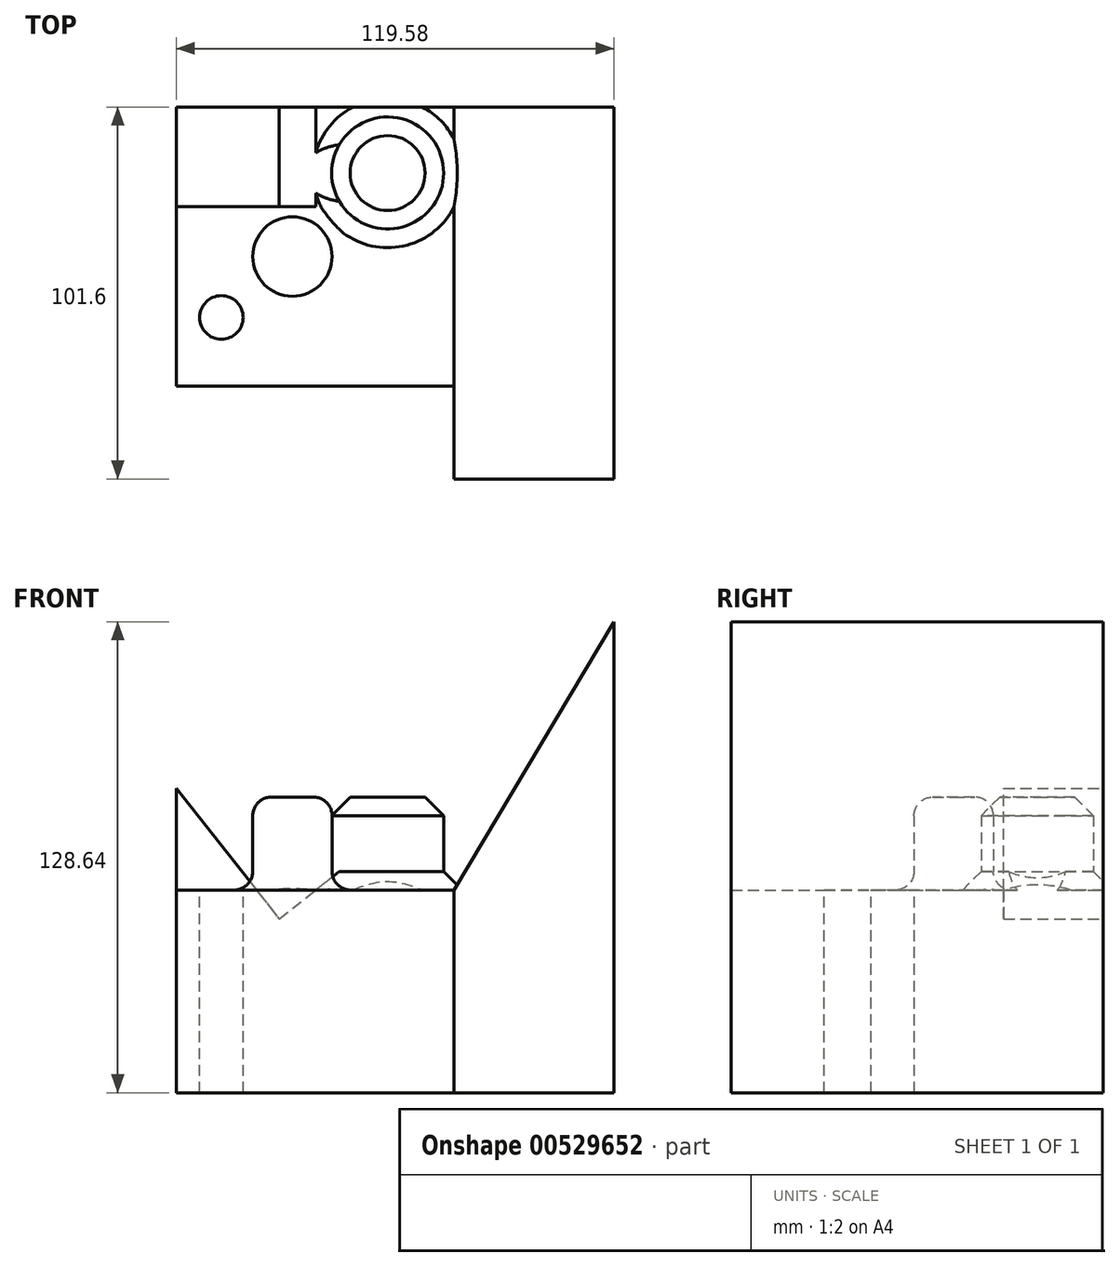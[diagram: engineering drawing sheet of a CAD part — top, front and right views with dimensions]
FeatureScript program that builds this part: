
annotation { "Feature Type Name" : "Feature", "Feature Type Description" : "" }
export const myFeature = defineFeature(function(context is Context, id is Id, definition is map)
    precondition{}
    {
        {
            var Q0;
            Q0=qCreatedBy(makeId("Front.planeOp"),FACE);
            var sketch = newSketch(context, id + "F0", { "sketchPlane" : qUnion([Q0])});
            skLineSegment(sketch, "E0", {"start": v(0, 0) * mm, "end": v(43.67, 73.3) * mm});
            skLineSegment(sketch, "E1", {"start": v(43.67, 73.3) * mm, "end": v(43.67, -55.35) * mm});
            skLineSegment(sketch, "E2", {"start": v(43.67, -55.35) * mm, "end": v(-75.9, -55.35) * mm});
            skLineSegment(sketch, "E3", {"start": v(-75.9, -55.35) * mm, "end": v(-75.9, 48.22) * mm});
            skLineSegment(sketch, "E4", {"start": v(-75.9, 48.22) * mm, "end": v(-37.8, 0) * mm});
            skLineSegment(sketch, "E5", {"start": v(-37.8, 0) * mm, "end": v(0, 0) * mm});
            skSolve(sketch);
        }
        {
            var Q0;
            Q0=makeQuery(id+"F0.imprint","IMPRINT",FACE,{"disambiguationData":[TD([[makeQuery(id+"F0.imprint","IMPRINT",EDGE,{"derivedFrom":sQuery(id+"F0.wireOp",EDGE,"E0")}),-1.0]])]});
            extrude(context, id + "F1", {"entities" : qUnion([Q0]), "depth" : 76.2 * mm, "offsetDistance" : 25.4 * mm});
        }
        {
            var Q0;
            Q0=makeQuery(id+"F1.opExtrude","CAP_FACE",FACE,{"disambiguationData":[OSD([sQuery(id+"F0.wireOp",EDGE,"E0"),sQuery(id+"F0.wireOp",EDGE,"E1"),sQuery(id+"F0.wireOp",EDGE,"E2"),sQuery(id+"F0.wireOp",EDGE,"E3"),sQuery(id+"F0.wireOp",EDGE,"E4"),sQuery(id+"F0.wireOp",EDGE,"E5")])],"isStart":false});
            var sketch = newSketch(context, id + "F2", { "sketchPlane" : qUnion([Q0])});
            skLineSegment(sketch, "E6", {"start": v(0, 0) * mm, "end": v(0, -55.35) * mm});
            skLineSegment(sketch, "E7", {"start": v(-37.8, 0) * mm, "end": v(-75.9, 0) * mm});
            skSolve(sketch);
        }
        {
            var Q0;
            {var subQ0=sQuery(id+"F2.wireOp",EDGE,"E6");Q0=makeQuery(id+"F2.imprint","IMPRINT",FACE,{"disambiguationData":[TD([[makeQuery(id+"F2.imprint","IMPRINT",EDGE,{"derivedFrom":subQ0}),1.0]])]});}
            extrude(context, id + "F3", {"entities" : qUnion([Q0]), "operationType" : NewBodyOperationType.ADD, "depth" : 25.4 * mm, "offsetDistance" : 25.4 * mm});
        }
        {
            var Q0;
            Q0=makeQuery(id+"F1.opExtrude","CAP_FACE",FACE,{"disambiguationData":[OSD([sQuery(id+"F0.wireOp",EDGE,"E0"),sQuery(id+"F0.wireOp",EDGE,"E1"),sQuery(id+"F0.wireOp",EDGE,"E2"),sQuery(id+"F0.wireOp",EDGE,"E3"),sQuery(id+"F0.wireOp",EDGE,"E4"),sQuery(id+"F0.wireOp",EDGE,"E5")])],"isStart":false});
            var sketch = newSketch(context, id + "F4", { "sketchPlane" : qUnion([Q0])});
            skLineSegment(sketch, "E8", {"start": v(-37.8, 0) * mm, "end": v(-75.9, 0) * mm});
            skSolve(sketch);
        }
        {
            var Q0;
            {var subQ0=sQuery(id+"F4.wireOp",EDGE,"E8");Q0=makeQuery(id+"F4.imprint","IMPRINT",FACE,{"disambiguationData":[TD([[makeQuery(id+"F4.imprint","IMPRINT",EDGE,{"derivedFrom":subQ0}),-1.0]])]});}
            extrude(context, id + "F5", {"entities" : qUnion([Q0]), "operationType" : NewBodyOperationType.REMOVE, "oppositeDirection" : true, "depth" : 49.02 * mm, "offsetDistance" : 25.4 * mm});
        }
        {
            var Q0;
            Q0=makeQuery(id+"F5.boolean.opBoolean","MERGE",FACE,{"derivedFrom":[makeQuery(id+"F1.opExtrude","SWEPT_FACE",FACE,{"disambiguationData":[OSD([sQuery(id+"F0.wireOp",EDGE,"E5")])]}),makeQuery(id+"F5.opExtrude","SWEPT_FACE",FACE,{"disambiguationData":[OSD([sQuery(id+"F4.wireOp",EDGE,"E8")])]})]});
            var sketch = newSketch(context, id + "F6", { "sketchPlane" : qUnion([Q0])});
            skCircle(sketch, "E9", {"center": v(-44.18, -40.85) * mm, "radius": 10.84 * mm});
            skCircle(sketch, "E10", {"center": v(-18.17, -18.04) * mm, "radius": 15.3 * mm});
            skCircle(sketch, "E11", {"center": v(-63.59, -57.5) * mm, "radius": 5.95 * mm});
            skSolve(sketch);
        }
        {
            var Q0;
            Q0=makeQuery(id+"F6.imprint","IMPRINT",FACE,{"disambiguationData":[TD([[makeQuery(id+"F6.imprint","IMPRINT",EDGE,{"derivedFrom":sQuery(id+"F6.wireOp",EDGE,"E10")}),1.0]])]});
            var Q1;
            Q1=makeQuery(id+"F6.imprint","IMPRINT",FACE,{"disambiguationData":[TD([[makeQuery(id+"F6.imprint","IMPRINT",EDGE,{"derivedFrom":sQuery(id+"F6.wireOp",EDGE,"E9")}),1.0]])]});
            var Q2;
            Q2=makeQuery(id+"F6.imprint","IMPRINT",FACE,{"disambiguationData":[TD([[makeQuery(id+"F6.imprint","IMPRINT",EDGE,{"derivedFrom":sQuery(id+"F6.wireOp",EDGE,"E11")}),1.0]])]});
            extrude(context, id + "F7", {"entities" : qUnion([Q0, Q1, Q2]), "operationType" : NewBodyOperationType.ADD, "depth" : 25.4 * mm, "offsetDistance" : 25.4 * mm});
        }
        {
            var Q0;
            Q0=makeQuery(id+"F1.opExtrude","SWEPT_FACE",FACE,{"disambiguationData":[OSD([sQuery(id+"F0.wireOp",EDGE,"E4")])]});
            extrude(context, id + "F8", {"entities" : qUnion([Q0]), "operationType" : NewBodyOperationType.REMOVE, "oppositeDirection" : true, "depth" : 12.7 * mm, "offsetDistance" : 25.4 * mm});
        }
        {
            var Q0;
            Q0=makeQuery(id+"F7.opExtrude","CAP_FACE",FACE,{"disambiguationData":[OSD([sQuery(id+"F6.wireOp",EDGE,"E11")])],"isStart":false});
            extrude(context, id + "F9", {"entities" : qUnion([Q0]), "operationType" : NewBodyOperationType.REMOVE, "oppositeDirection" : true, "depth" : 120.4 * mm, "offsetDistance" : 25.4 * mm});
        }
        {
            var Q0;
            Q0=makeQuery(id+"F7.opExtrude","SWEPT_FACE",FACE,{"disambiguationData":[OSD([sQuery(id+"F6.wireOp",EDGE,"E9")])]});
            fillet(context, id + "F10", {"entities" : qUnion([Q0]), "radius" : 5.08 * mm, "tangentPropagation" : true, "allowEdgeOverflow" : false});
        }
        {
            var Q0;
            Q0=makeQuery(id+"F7.opExtrude","SWEPT_FACE",FACE,{"disambiguationData":[OSD([sQuery(id+"F6.wireOp",EDGE,"E10")])]});
            chamfer(context, id + "F11", {"entities" : qUnion([Q0]), "width" : 5.08 * mm, "tangentPropagation" : true});
        }
    });
